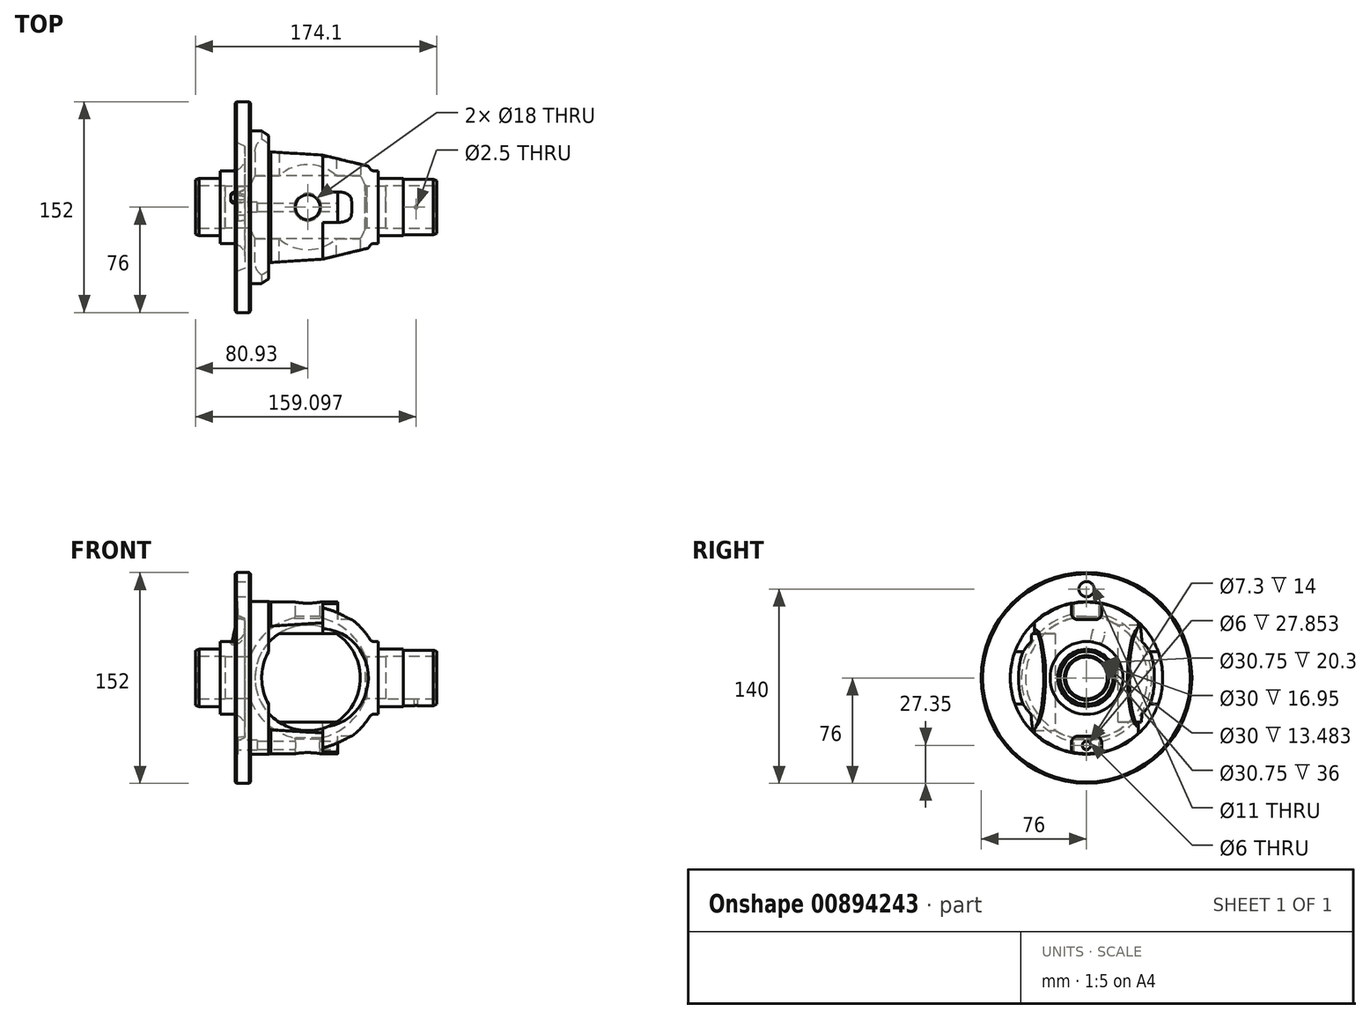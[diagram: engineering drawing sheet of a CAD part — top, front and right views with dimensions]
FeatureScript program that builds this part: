
annotation { "Feature Type Name" : "Feature", "Feature Type Description" : "" }
export const myFeature = defineFeature(function(context is Context, id is Id, definition is map)
    precondition{}
    {
        {
            var Q0;
            Q0=qCreatedBy(makeId("Front.planeOp"),FACE);
            var sketch = newSketch(context, id + "F0", { "sketchPlane" : qUnion([Q0])});
            skLineSegment(sketch, "E0", {"start": v(50.77, 21.18) * mm, "end": v(50.77, 26.25) * mm});
            skLineSegment(sketch, "E1", {"start": v(50.77, 26.25) * mm, "end": v(47.47, 26.25) * mm});
            skLineSegment(sketch, "E2", {"start": v(-78.43, 20.67) * mm, "end": v(-63.73, 20.67) * mm});
            skLineSegment(sketch, "E3", {"start": v(-63.23, 21.17) * mm, "end": v(-63.23, 26.25) * mm});
            skLineSegment(sketch, "E4", {"start": v(-63.23, 26.25) * mm, "end": v(-54.33, 26.25) * mm});
            skLineSegment(sketch, "E5", {"start": v(-41.23, 75) * mm, "end": v(-41.23, 55.5) * mm});
            skLineSegment(sketch, "E6", {"start": v(-40.73, 55) * mm, "end": v(-28.23, 55) * mm});
            skLineSegment(sketch, "E7", {"start": v(-79.93, 15.37) * mm, "end": v(-59.63, 15.37) * mm});
            skLineSegment(sketch, "E8", {"start": v(90.67, 20) * mm, "end": v(93.17, 19) * mm});
            skLineSegment(sketch, "E9", {"start": v(93.17, 16.03) * mm, "end": v(92.17, 15.38) * mm});
            skLineSegment(sketch, "E10", {"start": v(92.17, 15.38) * mm, "end": v(56.17, 15.38) * mm});
            skLineSegment(sketch, "E11", {"start": v(56.17, 15) * mm, "end": v(56.17, 15.38) * mm});
            skLineSegment(sketch, "E12", {"start": v(56.17, 15) * mm, "end": v(41.68, 15) * mm});
            skLineSegment(sketch, "E13", {"start": v(93.17, 19) * mm, "end": v(93.17, 16.03) * mm});
            skLineSegment(sketch, "E14", {"start": v(90.67, 20) * mm, "end": v(68.87, 20) * mm});
            skLineSegment(sketch, "E15", {"start": v(68.87, 20) * mm, "end": v(68.87, 20.68) * mm});
            skLineSegment(sketch, "E16", {"start": v(68.87, 20.68) * mm, "end": v(51.27, 20.68) * mm});
            skLineSegment(sketch, "E17", {"start": v(-78.43, 20.67) * mm, "end": v(-80.93, 19.67) * mm});
            skLineSegment(sketch, "E18", {"start": v(-80.93, 19.67) * mm, "end": v(-80.93, 16.02) * mm});
            skLineSegment(sketch, "E19", {"start": v(-80.93, 16.02) * mm, "end": v(-79.93, 15.37) * mm});
            skLineSegment(sketch, "E20", {"start": v(-45.33, 35.25) * mm, "end": v(-45.33, 44) * mm});
            skLineSegment(sketch, "E21", {"start": v(-52.33, 47) * mm, "end": v(-52.33, 75) * mm});
            skLineSegment(sketch, "E22", {"start": v(-59.63, 15.37) * mm, "end": v(-59.63, 15) * mm});
            skLineSegment(sketch, "E23", {"start": v(-59.63, 15) * mm, "end": v(-41.68, 15) * mm});
            skLineSegment(sketch, "E24", {"start": v(-52.33, 47) * mm, "end": v(-45.33, 44) * mm});
            skPoint(sketch, "E25.visualSharp", {"position": v(-45.33, 26.25) * mm});
            skArc(sketch, "E25.filletArc", {"start": v(-54.33, 26.25) * mm, "mid": v(-47.97, 28.89) * mm, "end": v(-45.33, 35.25) * mm});
            skLineSegment(sketch, "E26", {"start": v(-28.23, 55) * mm, "end": v(-26.73, 54.65) * mm});
            skLineSegment(sketch, "E27", {"start": v(-26.73, 54.65) * mm, "end": v(10.77, 54.65) * mm});
            skLineSegment(sketch, "E28", {"start": v(10.77, 54.65) * mm, "end": v(10.77, 52.86) * mm});
            skArc(sketch, "E29", {"start": v(44.92, 27.68) * mm, "mid": v(30.8, 42.84) * mm, "end": v(11.93, 51.4) * mm});
            skLineSegment(sketch, "E30", {"start": v(-52.33, 75) * mm, "end": v(-51.33, 76) * mm});
            skLineSegment(sketch, "E31", {"start": v(-51.33, 76) * mm, "end": v(-42.23, 76) * mm});
            skLineSegment(sketch, "E32", {"start": v(-42.23, 76) * mm, "end": v(-41.23, 75) * mm});
            skPoint(sketch, "E33.visualSharp", {"position": v(-41.23, 55) * mm});
            skArc(sketch, "E33.filletArc", {"start": v(-41.23, 55.5) * mm, "mid": v(-41.09, 55.15) * mm, "end": v(-40.73, 55) * mm});
            skPoint(sketch, "E34.visualSharp", {"position": v(-63.23, 20.67) * mm});
            skArc(sketch, "E34.filletArc", {"start": v(-63.73, 20.67) * mm, "mid": v(-63.38, 20.82) * mm, "end": v(-63.23, 21.17) * mm});
            skPoint(sketch, "E35.visualSharp", {"position": v(50.77, 20.68) * mm});
            skArc(sketch, "E35.filletArc", {"start": v(50.77, 21.18) * mm, "mid": v(50.91, 20.82) * mm, "end": v(51.27, 20.68) * mm});
            skPoint(sketch, "E36.visualSharp", {"position": v(10.77, 51.65) * mm});
            skArc(sketch, "E36.filletArc", {"start": v(10.77, 52.86) * mm, "mid": v(11.1, 51.92) * mm, "end": v(11.93, 51.4) * mm});
            skPoint(sketch, "E37.visualSharp", {"position": v(45.77, 26.25) * mm});
            skArc(sketch, "E37.filletArc", {"start": v(44.92, 27.68) * mm, "mid": v(46, 26.63) * mm, "end": v(47.47, 26.25) * mm});
            skArc(sketch, "E38", {"start": v(41.68, 15) * mm, "mid": v(0, 44.3) * mm, "end": v(-41.68, 15) * mm});
            skLineSegment(sketch, "E39", {"start": v(-80.93, 0) * mm, "end": v(93.17, 0) * mm});
            skSolve(sketch);
        }
        {
            var Q0;
            Q0=makeQuery(id+"F0.imprint","IMPRINT",FACE,{"disambiguationData":[TD([[makeQuery(id+"F0.imprint","IMPRINT",EDGE,{"derivedFrom":sQuery(id+"F0.wireOp",EDGE,"E0")}),1.0]])]});
            var Q1;
            Q1=sQuery(id+"F0.wireOp",EDGE,"E39");
            revolve(context, id + "F1", {"surfaceOperationType" : NewSurfaceOperationType.NEW, "entities" : qUnion([Q0]), "axis" : qUnion([Q1]), "revolveType" : RevolveType.FULL});
        }
        {
            var Q0;
            Q0=qCreatedBy(makeId("Front.planeOp"),FACE);
            var sketch = newSketch(context, id + "F2", { "sketchPlane" : qUnion([Q0])});
            skLineSegment(sketch, "E40", {"start": v(-20.66, -31.95) * mm, "end": v(20.66, -31.95) * mm});
            skLineSegment(sketch, "E41", {"start": v(0, 0) * mm, "end": v(0, -31.95) * mm, "construction": true});
            skArc(sketch, "E42", {"start": v(20.66, -31.95) * mm, "mid": v(0, 38.05) * mm, "end": v(-20.66, -31.95) * mm});
            skSolve(sketch);
        }
        {
            var Q0;
            Q0 = qSketchRegion(id + "F2", true);
            extrude(context, id + "F3", {"entities" : qUnion([Q0]), "operationType" : NewBodyOperationType.REMOVE, "oppositeDirection" : true, "depth" : 40 * mm, "offsetDistance" : 25 * mm});
        }
        {
            var Q0;
            Q0=qCreatedBy(makeId("Top.planeOp"),FACE);
            var sketch = newSketch(context, id + "F4", { "sketchPlane" : qUnion([Q0])});
            skLineSegment(sketch, "E43", {"start": v(-28.23, 55) * mm, "end": v(-28.23, 40.94) * mm});
            skLineSegment(sketch, "E44", {"start": v(-27.3, 39.94) * mm, "end": v(10.77, 37.5) * mm});
            skLineSegment(sketch, "E45", {"start": v(10.77, 37.5) * mm, "end": v(44.92, 29.25) * mm});
            skLineSegment(sketch, "E46", {"start": v(-28.23, 55) * mm, "end": v(44.92, 55) * mm});
            skLineSegment(sketch, "E47", {"start": v(44.92, 55) * mm, "end": v(44.92, 29.25) * mm});
            skLineSegment(sketch, "E48.MirrorCS", {"start": v(44.92, -55) * mm, "end": v(44.92, -29.25) * mm});
            skLineSegment(sketch, "E49.MirrorCS", {"start": v(-28.23, -55) * mm, "end": v(44.92, -55) * mm});
            skLineSegment(sketch, "E50.MirrorCS", {"start": v(-28.23, -55) * mm, "end": v(-28.23, -40.94) * mm});
            skLineSegment(sketch, "E51.MirrorCS", {"start": v(-27.3, -39.94) * mm, "end": v(10.77, -37.5) * mm});
            skLineSegment(sketch, "E52.MirrorCS", {"start": v(10.77, -37.5) * mm, "end": v(44.92, -29.25) * mm});
            skPoint(sketch, "E53.visualSharp", {"position": v(-28.23, 40) * mm});
            skArc(sketch, "E53.filletArc", {"start": v(-28.23, 40.94) * mm, "mid": v(-27.96, 40.25) * mm, "end": v(-27.3, 39.94) * mm});
            skPoint(sketch, "E54.visualSharp", {"position": v(-28.23, -40) * mm});
            skArc(sketch, "E54.filletArc", {"start": v(-27.3, -39.94) * mm, "mid": v(-27.96, -40.25) * mm, "end": v(-28.23, -40.94) * mm});
            skSolve(sketch);
        }
        {
            var Q0;
            Q0 = qSketchRegion(id + "F4", true);
            extrude(context, id + "F5", {"entities" : qUnion([Q0]), "operationType" : NewBodyOperationType.REMOVE, "oppositeDirection" : true, "depth" : 80 * mm, "offsetDistance" : 25 * mm, "symmetric" : true});
        }
        {
            var Q0;
            Q0=qCreatedBy(makeId("Front.planeOp"),FACE);
            var sketch = newSketch(context, id + "F6", { "sketchPlane" : qUnion([Q0])});
            skLineSegment(sketch, "E55", {"start": v(-28.23, 18.85) * mm, "end": v(-28.23, -18.85) * mm});
            skArc(sketch, "E56", {"start": v(-28.23, 18.85) * mm, "mid": v(-33.23, 0) * mm, "end": v(-28.23, -18.85) * mm});
            skSolve(sketch);
        }
        {
            var Q0;
            Q0 = qSketchRegion(id + "F6", true);
            extrude(context, id + "F7", {"entities" : qUnion([Q0]), "operationType" : NewBodyOperationType.REMOVE, "oppositeDirection" : true, "depth" : 110 * mm, "offsetDistance" : 25 * mm, "symmetric" : true});
        }
        {
            var Q0;
            Q0=qCreatedBy(makeId("Front.planeOp"),FACE);
            cPlane(context, id + "F8", {"entities" : qUnion([Q0]), "cplaneType" : CPlaneType.OFFSET, "offset" : 40 * mm, "oppositeDirection" : true, "width" : 150 * mm, "height" : 150 * mm});
        }
        {
            var Q0;
            Q0=qCreatedBy(id+"F8.planeOp",FACE);
            var sketch = newSketch(context, id + "F9", { "sketchPlane" : qUnion([Q0])});
            skArc(sketch, "E57.0", {"start": v(-27.3, 26.5) * mm, "mid": v(-38.05, 0) * mm, "end": v(-27.3, -26.5) * mm});
            skLineSegment(sketch, "E58", {"start": v(-27.3, -26.5) * mm, "end": v(-27.3, 26.5) * mm});
            skSolve(sketch);
        }
        {
            var Q0;
            Q0=makeQuery(id+"F9.imprint","IMPRINT",FACE,{"disambiguationData":[TD([[makeQuery(id+"F9.imprint","IMPRINT",EDGE,{"derivedFrom":sQuery(id+"F9.wireOp",EDGE,"E57.0")}),1.0]])]});
            var Q1;
            Q1=sQuery(id+"F9.wireOp",EDGE,"E58");
            revolve(context, id + "F10", {"operationType" : NewBodyOperationType.REMOVE, "surfaceOperationType" : NewSurfaceOperationType.NEW, "entities" : qUnion([Q0]), "axis" : qUnion([Q1]), "revolveType" : RevolveType.ONE_DIRECTION, "oppositeDirection" : true, "angle" : 90 * degree});
        }
        {
            var Q0;
            Q0=qCreatedBy(makeId("Front.planeOp"),FACE);
            var sketch = newSketch(context, id + "F11", { "sketchPlane" : qUnion([Q0])});
            skArc(sketch, "E59", {"start": v(-20.66, 31.95) * mm, "mid": v(0, -38.05) * mm, "end": v(20.66, 31.95) * mm});
            skLineSegment(sketch, "E60", {"start": v(0, 0) * mm, "end": v(0, 31.95) * mm, "construction": true});
            skLineSegment(sketch, "E61", {"start": v(20.66, 31.95) * mm, "end": v(-20.66, 31.95) * mm});
            skSolve(sketch);
        }
        {
            var Q0;
            Q0 = qSketchRegion(id + "F11", true);
            extrude(context, id + "F12", {"entities" : qUnion([Q0]), "operationType" : NewBodyOperationType.REMOVE, "depth" : 40 * mm, "offsetDistance" : 25 * mm});
        }
        {
            var Q0;
            Q0=qCreatedBy(makeId("Front.planeOp"),FACE);
            cPlane(context, id + "F13", {"entities" : qUnion([Q0]), "cplaneType" : CPlaneType.OFFSET, "offset" : 40 * mm, "width" : 150 * mm, "height" : 150 * mm});
        }
        {
            var Q0;
            Q0=qCreatedBy(id+"F13.planeOp",FACE);
            var sketch = newSketch(context, id + "F14", { "sketchPlane" : qUnion([Q0])});
            skLineSegment(sketch, "E62", {"start": v(-27.3, 26.5) * mm, "end": v(-27.3, -26.5) * mm});
            skArc(sketch, "E63", {"start": v(-27.3, 26.5) * mm, "mid": v(-38.05, 0) * mm, "end": v(-27.3, -26.5) * mm});
            skSolve(sketch);
        }
        {
            var Q0;
            Q0 = qSketchRegion(id + "F14", true);
            var Q1;
            Q1=sQuery(id+"F14.wireOp",EDGE,"E62");
            revolve(context, id + "F15", {"operationType" : NewBodyOperationType.REMOVE, "surfaceOperationType" : NewSurfaceOperationType.NEW, "entities" : qUnion([Q0]), "axis" : qUnion([Q1]), "revolveType" : RevolveType.ONE_DIRECTION, "oppositeDirection" : true, "angle" : 90 * degree});
        }
        {
            var Q0;
            Q0=makeQuery(id+"F1.opRevolve","SWEPT_FACE",FACE,{"disambiguationData":[OSD([sQuery(id+"F0.wireOp",EDGE,"E5")])]});
            var sketch = newSketch(context, id + "F16", { "sketchPlane" : qUnion([Q0])});
            skCircle(sketch, "E64", {"center": v(0, 64) * mm, "radius": 5.5 * mm});
            skSolve(sketch);
        }
        {
            var Q0;
            Q0 = qSketchRegion(id + "F16", true);
            extrude(context, id + "F17", {"entities" : qUnion([Q0]), "operationType" : NewBodyOperationType.REMOVE, "oppositeDirection" : true, "depth" : 11.1 * mm, "offsetDistance" : 25 * mm});
        }
        {
            var Q0;
            Q0=qCreatedBy(makeId("Top.planeOp"),FACE);
            var sketch = newSketch(context, id + "F18", { "sketchPlane" : qUnion([Q0])});
            skCircle(sketch, "E65", {"center": v(0, 0) * mm, "radius": 9 * mm});
            skSolve(sketch);
        }
        {
            var Q0;
            Q0 = qSketchRegion(id + "F18", true);
            extrude(context, id + "F19", {"entities" : qUnion([Q0]), "operationType" : NewBodyOperationType.REMOVE, "oppositeDirection" : true, "depth" : 110 * mm, "offsetDistance" : 25 * mm, "symmetric" : true});
        }
        {
            var Q0;
            Q0=makeQuery(id+"F5.boolean.opBoolean","SPLIT",FACE,{"disambiguationData":[OD(1.0)],"derivedFrom":makeQuery(id+"F1.opRevolve","SWEPT_FACE",FACE,{"disambiguationData":[OSD([sQuery(id+"F0.wireOp",EDGE,"E28")])]})});
            var sketch = newSketch(context, id + "F20", { "sketchPlane" : qUnion([Q0])});
            skLineSegment(sketch, "E66", {"start": v(11, 53.53) * mm, "end": v(11, 43) * mm});
            skLineSegment(sketch, "E67", {"start": v(11, 43) * mm, "end": v(-11, 43) * mm});
            skLineSegment(sketch, "E68", {"start": v(-11, 43) * mm, "end": v(-11, 53.53) * mm});
            skArc(sketch, "E69", {"start": v(11, 53.53) * mm, "mid": v(0, 54.65) * mm, "end": v(-11, 53.53) * mm});
            skPoint(sketch, "E70.visualSharp", {"position": v(-11, 43) * mm});
            skPoint(sketch, "E71.visualSharp", {"position": v(11, 43) * mm});
            skLineSegment(sketch, "E72", {"start": v(-10.57, 0) * mm, "end": v(10.57, 0) * mm, "construction": true});
            skLineSegment(sketch, "E73.MirrorCS", {"start": v(11, -43) * mm, "end": v(11, -43) * mm});
            skLineSegment(sketch, "E74.MirrorCS", {"start": v(11, -43) * mm, "end": v(-11, -43) * mm});
            skLineSegment(sketch, "E75.MirrorCS", {"start": v(-11, -43) * mm, "end": v(-11, -43) * mm});
            skLineSegment(sketch, "E76.MirrorCS", {"start": v(-11, -43) * mm, "end": v(-11, -53.53) * mm});
            skArc(sketch, "E77.MirrorCS", {"start": v(11, -53.53) * mm, "mid": v(0, -54.65) * mm, "end": v(-11, -53.53) * mm});
            skLineSegment(sketch, "E78.MirrorCS", {"start": v(11, -53.53) * mm, "end": v(11, -43) * mm});
            skSolve(sketch);
        }
        {
            var Q0;
            Q0 = qSketchRegion(id + "F20", true);
            extrude(context, id + "F21", {"entities" : qUnion([Q0]), "operationType" : NewBodyOperationType.ADD, "depth" : 11 * mm, "offsetDistance" : 25 * mm});
        }
        {
            var Q0;
            Q0=makeQuery(id+"F21.opExtrude","CAP_FACE",FACE,{"disambiguationData":[OSD([sQuery(id+"F20.wireOp",EDGE,"E66"),sQuery(id+"F20.wireOp",EDGE,"E67"),sQuery(id+"F20.wireOp",EDGE,"E68"),sQuery(id+"F20.wireOp",EDGE,"E69")])],"isStart":false});
            var sketch = newSketch(context, id + "F22", { "sketchPlane" : qUnion([Q0])});
            skLineSegment(sketch, "E79", {"start": v(6.22, 42) * mm, "end": v(-6.21, 42) * mm});
            skLineSegment(sketch, "E80", {"start": v(11, 46.79) * mm, "end": v(11, 46.79) * mm});
            skLineSegment(sketch, "E81", {"start": v(-11, 46.78) * mm, "end": v(-11, 46.79) * mm});
            skArc(sketch, "E82.filletArc", {"start": v(-11, 46.78) * mm, "mid": v(-9.6, 43.4) * mm, "end": v(-6.21, 42) * mm});
            skArc(sketch, "E83.filletArc", {"start": v(6.22, 42) * mm, "mid": v(9.6, 43.4) * mm, "end": v(11, 46.79) * mm});
            skArc(sketch, "E84.0", {"start": v(11, 46.79) * mm, "mid": v(0, 48.06) * mm, "end": v(-11, 46.79) * mm});
            skArc(sketch, "E85.MirrorCS", {"start": v(11, -46.79) * mm, "mid": v(0, -48.06) * mm, "end": v(-11, -46.79) * mm});
            skLineSegment(sketch, "E86", {"start": v(-6.21, -42) * mm, "end": v(6.21, -42) * mm});
            skLineSegment(sketch, "E87", {"start": v(11, -46.79) * mm, "end": v(11, -46.79) * mm});
            skLineSegment(sketch, "E88", {"start": v(-11, -46.79) * mm, "end": v(-11, -46.79) * mm});
            skPoint(sketch, "E89.visualSharp", {"position": v(-11, -42) * mm});
            skArc(sketch, "E89.filletArc", {"start": v(-6.21, -42) * mm, "mid": v(-9.6, -43.4) * mm, "end": v(-11, -46.79) * mm});
            skPoint(sketch, "E90.visualSharp", {"position": v(11, -42) * mm});
            skArc(sketch, "E90.filletArc", {"start": v(11, -46.79) * mm, "mid": v(9.6, -43.4) * mm, "end": v(6.21, -42) * mm});
            skSolve(sketch);
        }
        {
            var Q0;
            Q0 = qSketchRegion(id + "F22", true);
            extrude(context, id + "F23", {"entities" : qUnion([Q0]), "operationType" : NewBodyOperationType.REMOVE, "depth" : 12 * mm, "offsetDistance" : 25 * mm});
        }
        {
            var Q0;
            Q0=makeQuery(id+"F23.boolean.opBoolean","MERGE",FACE,{"derivedFrom":[makeQuery(id+"F21.opExtrude","CAP_FACE",FACE,{"disambiguationData":[OSD([sQuery(id+"F20.wireOp",EDGE,"E74.MirrorCS"),sQuery(id+"F20.wireOp",EDGE,"E76.MirrorCS"),sQuery(id+"F20.wireOp",EDGE,"E77.MirrorCS"),sQuery(id+"F20.wireOp",EDGE,"E78.MirrorCS")])],"isStart":false})],"fromTools":[makeQuery(id+"F23.opExtrude","CAP_FACE",FACE,{"disambiguationData":[OSD([sQuery(id+"F22.wireOp",EDGE,"E85.MirrorCS"),sQuery(id+"F22.wireOp",EDGE,"E86"),sQuery(id+"F22.wireOp",EDGE,"E87"),sQuery(id+"F22.wireOp",EDGE,"E88"),sQuery(id+"F22.wireOp",EDGE,"E89.filletArc"),sQuery(id+"F22.wireOp",EDGE,"E90.filletArc")])],"isStart":true})]});
            var sketch = newSketch(context, id + "F24", { "sketchPlane" : qUnion([Q0])});
            skCircle(sketch, "E91", {"center": v(0, -48.65) * mm, "radius": 3 * mm});
            skSolve(sketch);
        }
        {
            var Q0;
            Q0 = qSketchRegion(id + "F24", true);
            extrude(context, id + "F25", {"entities" : qUnion([Q0]), "operationType" : NewBodyOperationType.REMOVE, "endBound" : BoundingType.THROUGH_ALL, "oppositeDirection" : true, "depth" : 25 * mm, "offsetDistance" : 25 * mm});
        }
        {
            var Q0;
            Q0=makeQuery(id+"F1.opRevolve","SWEPT_FACE",FACE,{"disambiguationData":[OSD([sQuery(id+"F0.wireOp",EDGE,"E21")])]});
            var sketch = newSketch(context, id + "F26", { "sketchPlane" : qUnion([Q0])});
            skCircle(sketch, "E92", {"center": v(0, -48.65) * mm, "radius": 3.65 * mm});
            skSolve(sketch);
        }
        {
            var Q0;
            Q0 = qSketchRegion(id + "F26", true);
            extrude(context, id + "F27", {"entities" : qUnion([Q0]), "operationType" : NewBodyOperationType.REMOVE, "oppositeDirection" : true, "depth" : 16 * mm, "offsetDistance" : 25 * mm});
        }
        {
            var Q0;
            Q0=qCreatedBy(makeId("Top.planeOp"),FACE);
            var sketch = newSketch(context, id + "F28", { "sketchPlane" : qUnion([Q0])});
            skCircle(sketch, "E93", {"center": v(78.17, 0) * mm, "radius": 1.25 * mm});
            skSolve(sketch);
        }
        {
            var Q0;
            Q0 = qSketchRegion(id + "F28", true);
            extrude(context, id + "F29", {"entities" : qUnion([Q0]), "operationType" : NewBodyOperationType.REMOVE, "endBound" : BoundingType.THROUGH_ALL, "oppositeDirection" : true, "depth" : 25 * mm, "offsetDistance" : 25 * mm});
        }
        {
            var Q0;
            Q0=makeQuery(id+"F1.opRevolve","SWEPT_FACE",FACE,{"disambiguationData":[OSD([sQuery(id+"F0.wireOp",EDGE,"E21")])]});
            var sketch = newSketch(context, id + "F30", { "sketchPlane" : qUnion([Q0])});
            skLineSegment(sketch, "E94.0", {"start": v(-6.22, 42) * mm, "end": v(6.21, 42) * mm});
            skArc(sketch, "E95.0", {"start": v(6.21, 42) * mm, "mid": v(9.6, 43.4) * mm, "end": v(11, 46.78) * mm});
            skArc(sketch, "E96.0", {"start": v(-11, 46.79) * mm, "mid": v(-9.6, 43.4) * mm, "end": v(-6.22, 42) * mm});
            skLineSegment(sketch, "E97.0", {"start": v(-11, 53.53) * mm, "end": v(-11, 46.79) * mm});
            skLineSegment(sketch, "E98.0", {"start": v(11, 46.79) * mm, "end": v(11, 53.53) * mm});
            skLineSegment(sketch, "E99.0", {"start": v(6.21, -42) * mm, "end": v(-6.21, -42) * mm});
            skArc(sketch, "E100.0", {"start": v(-6.21, -42) * mm, "mid": v(-9.6, -43.4) * mm, "end": v(-11, -46.79) * mm});
            skArc(sketch, "E101.0", {"start": v(11, -46.78) * mm, "mid": v(9.6, -43.4) * mm, "end": v(6.21, -42) * mm});
            skLineSegment(sketch, "E102.0", {"start": v(11, -46.79) * mm, "end": v(11, -53.53) * mm});
            skLineSegment(sketch, "E103.0", {"start": v(-11, -53.53) * mm, "end": v(-11, -46.79) * mm});
            skLineSegment(sketch, "E104", {"start": v(-11, 53.53) * mm, "end": v(11, 53.53) * mm});
            skLineSegment(sketch, "E105", {"start": v(-11, -53.53) * mm, "end": v(11, -53.53) * mm});
            skArc(sketch, "E106.0", {"start": v(-3.2, -46.9) * mm, "mid": v(0, -52.3) * mm, "end": v(3.2, -46.9) * mm});
            skArc(sketch, "E107.0", {"start": v(3.2, -46.9) * mm, "mid": v(0, -45) * mm, "end": v(-3.2, -46.9) * mm});
            skSolve(sketch);
        }
        {
            var Q0;
            {var subQ0=sQuery(id+"F30.wireOp",EDGE,"E94.0");Q0=makeQuery(id+"F30.imprint","IMPRINT",FACE,{"disambiguationData":[TD([[makeQuery(id+"F30.imprint","IMPRINT",EDGE,{"derivedFrom":subQ0}),1.0]])]});}
            var Q1;
            {var subQ2=sQuery(id+"F30.wireOp",EDGE,"E99.0");Q1=makeQuery(id+"F30.imprint","IMPRINT",FACE,{"disambiguationData":[TD([[makeQuery(id+"F30.imprint","IMPRINT",EDGE,{"derivedFrom":subQ2}),1.0]])]});}
            var Q2;
            Q2=makeQuery(id+"F1.opRevolve","SWEPT_FACE",FACE,{"disambiguationData":[OSD([sQuery(id+"F0.wireOp",EDGE,"E20")])]});
            extrude(context, id + "F31", {"entities" : qUnion([Q0, Q1]), "operationType" : NewBodyOperationType.ADD, "endBound" : BoundingType.UP_TO_SURFACE, "oppositeDirection" : true, "depth" : 25 * mm, "endBoundEntityFace" : qUnion([Q2]), "offsetDistance" : 25 * mm});
        }
        {
            var Q0;
            Q0=makeQuery(id+"F31.opExtrude","CAP_EDGE",EDGE,{"disambiguationData":[OSD([sQuery(id+"F30.wireOp",EDGE,"E99.0")])],"isStart":true});
            var Q1;
            Q1=makeQuery(id+"F31.opExtrude","CAP_EDGE",EDGE,{"disambiguationData":[OSD([sQuery(id+"F30.wireOp",EDGE,"E94.0")])],"isStart":true});
            chamfer(context, id + "F32", {"entities" : qUnion([Q0, Q1]), "chamferType" : ChamferType.TWO_OFFSETS, "width1" : 1 * mm, "oppositeDirection" : false, "width2" : 7 * mm, "tangentPropagation" : true});
        }
        {
            var Q0;
            {var subQ0=sQuery(id+"F0.wireOp",EDGE,"E24");var subQ1=sQuery(id+"F0.wireOp",EDGE,"E21");Q0=makeQuery(id+"F31.boolean.opBoolean","MERGE",FACE,{"derivedFrom":[makeQuery(id+"F1.opRevolve","SWEPT_FACE",FACE,{"disambiguationData":[OSD([subQ1])]}),makeQuery(id+"F31.opExtrude","CAP_FACE",FACE,{"disambiguationData":[OSD([subQ1,subQ0,sQuery(id+"F30.wireOp",EDGE,"E94.0"),sQuery(id+"F30.wireOp",EDGE,"E95.0"),sQuery(id+"F30.wireOp",EDGE,"E96.0")])],"isStart":true}),makeQuery(id+"F31.opExtrude","CAP_FACE",FACE,{"disambiguationData":[OSD([subQ1,subQ0,sQuery(id+"F30.wireOp",EDGE,"E99.0"),sQuery(id+"F30.wireOp",EDGE,"E100.0"),sQuery(id+"F30.wireOp",EDGE,"E101.0"),sQuery(id+"F30.wireOp",EDGE,"E107.0")])],"isStart":true})]});}
            var sketch = newSketch(context, id + "F33", { "sketchPlane" : qUnion([Q0])});
            skLineSegment(sketch, "E108", {"start": v(4.9, -55) * mm, "end": v(-4.9, -55) * mm});
            skLineSegment(sketch, "E109", {"start": v(9.9, -50) * mm, "end": v(9.9, -42) * mm});
            skLineSegment(sketch, "E110", {"start": v(-9.9, -50) * mm, "end": v(-9.9, -42) * mm});
            skLineSegment(sketch, "E111", {"start": v(-10.43, 0) * mm, "end": v(10.43, 0) * mm});
            skPoint(sketch, "E112.visualSharp", {"position": v(-9.9, -55) * mm});
            skArc(sketch, "E112.filletArc", {"start": v(-9.9, -50) * mm, "mid": v(-8.44, -53.54) * mm, "end": v(-4.9, -55) * mm});
            skPoint(sketch, "E113.visualSharp", {"position": v(9.9, -55) * mm});
            skArc(sketch, "E113.filletArc", {"start": v(4.9, -55) * mm, "mid": v(8.44, -53.54) * mm, "end": v(9.9, -50) * mm});
            skArc(sketch, "E114.MirrorCS", {"start": v(4.9, 55) * mm, "mid": v(8.44, 53.54) * mm, "end": v(9.9, 50) * mm});
            skLineSegment(sketch, "E115.MirrorCS", {"start": v(4.9, 55) * mm, "end": v(-4.9, 55) * mm});
            skArc(sketch, "E116.MirrorCS", {"start": v(-9.9, 50) * mm, "mid": v(-8.44, 53.54) * mm, "end": v(-4.9, 55) * mm});
            skLineSegment(sketch, "E117", {"start": v(9.9, -42) * mm, "end": v(-9.9, -42) * mm});
            skLineSegment(sketch, "E118.MirrorCS", {"start": v(9.9, 50) * mm, "end": v(9.9, 42) * mm});
            skLineSegment(sketch, "E119.MirrorCS", {"start": v(9.9, 42) * mm, "end": v(-9.9, 42) * mm});
            skLineSegment(sketch, "E120.MirrorCS", {"start": v(-9.9, 50) * mm, "end": v(-9.9, 42) * mm});
            skSolve(sketch);
        }
        {
            var Q0;
            Q0 = qSketchRegion(id + "F33", true);
            extrude(context, id + "F34", {"entities" : qUnion([Q0]), "operationType" : NewBodyOperationType.REMOVE, "oppositeDirection" : true, "depth" : 2 * mm, "offsetDistance" : 25 * mm});
        }
        {
            var Q0;
            Q0=qCreatedBy(makeId("Front.planeOp"),FACE);
            var sketch = newSketch(context, id + "F35", { "sketchPlane" : qUnion([Q0])});
            skLineSegment(sketch, "E121", {"start": v(0, 0) * mm, "end": v(-24.58, 0) * mm, "construction": true});
            skSolve(sketch);
        }
        {
            var Q0;
            Q0=sQuery(id+"F35.wireOp",EDGE,"E121");
            var Q1;
            Q1=qCreatedBy(id+"F13.planeOp",FACE);
            cPlane(context, id + "F36", {"entities" : qUnion([Q0, Q1]), "cplaneType" : CPlaneType.LINE_ANGLE, "offset" : 25 * mm, "angle" : 15 * degree, "width" : 150 * mm, "height" : 150 * mm});
        }
        {
            var Q0;
            Q0=qCreatedBy(id+"F36.planeOp",FACE);
            var sketch = newSketch(context, id + "F37", { "sketchPlane" : qUnion([Q0])});
            skLineSegment(sketch, "E122", {"start": v(54.73, 26.25) * mm, "end": v(50.33, 47) * mm});
            skSolve(sketch);
        }
        {
            var Q0;
            Q0=sQuery(id+"F35.wireOp",EDGE,"E121");
            var Q1;
            Q1=qCreatedBy(id+"F36.planeOp",FACE);
            cPlane(context, id + "F38", {"entities" : qUnion([Q0, Q1]), "cplaneType" : CPlaneType.LINE_ANGLE, "offset" : 25 * mm, "angle" : 90 * degree, "width" : 150 * mm, "height" : 150 * mm});
        }
        {
            var Q0;
            Q0=qCreatedBy(id+"F38.planeOp",FACE);
            cPlane(context, id + "F39", {"entities" : qUnion([Q0]), "cplaneType" : CPlaneType.OFFSET, "offset" : 26 * mm, "width" : 150 * mm, "height" : 150 * mm});
        }
        {
            var Q0;
            Q0=qCreatedBy(id+"F39.planeOp",FACE);
            var sketch = newSketch(context, id + "F40", { "sketchPlane" : qUnion([Q0])});
            skLineSegment(sketch, "E123", {"start": v(-54.73, -2.1) * mm, "end": v(-54.73, 2.1) * mm});
            skLineSegment(sketch, "E124", {"start": v(-53.84, 3.1) * mm, "end": v(-45.33, 4) * mm});
            skLineSegment(sketch, "E125", {"start": v(-53.84, -3.1) * mm, "end": v(-45.33, -4) * mm});
            skLineSegment(sketch, "E126", {"start": v(-45.33, -4) * mm, "end": v(-45.33, 4) * mm});
            skPoint(sketch, "E127.visualSharp", {"position": v(-54.73, 3) * mm});
            skArc(sketch, "E127.filletArc", {"start": v(-53.84, 3.1) * mm, "mid": v(-54.48, 2.77) * mm, "end": v(-54.73, 2.1) * mm});
            skPoint(sketch, "E128.visualSharp", {"position": v(-54.73, -3) * mm});
            skArc(sketch, "E128.filletArc", {"start": v(-54.73, -2.1) * mm, "mid": v(-54.48, -2.77) * mm, "end": v(-53.84, -3.1) * mm});
            skSolve(sketch);
        }
        {
            var Q0;
            Q0 = qSketchRegion(id + "F40", true);
            var Q1;
            Q1=sQuery(id+"F37.wireOp",EDGE,"E122");
            sweep(context, id + "F41", {"operationType" : NewBodyOperationType.ADD, "profiles" : qUnion([Q0]), "path" : qUnion([Q1])});
        }
        {
            var Q0;
            Q0=makeQuery(id+"F41.boolean.opBoolean","INTERSECT",EDGE,{"derivedFrom":[makeQuery(id+"F1.opRevolve","SWEPT_FACE",FACE,{"disambiguationData":[OSD([sQuery(id+"F0.wireOp",EDGE,"E20")])]}),makeQuery(id+"F41.opSweep","SWEPT_FACE",FACE,{"disambiguationData":[OSD([sQuery(id+"F37.wireOp",EDGE,"E122"),sQuery(id+"F40.wireOp",EDGE,"E125")])]})]});
            var Q1;
            Q1=makeQuery(id+"F41.boolean.opBoolean","INTERSECT",EDGE,{"derivedFrom":[makeQuery(id+"F1.opRevolve","SWEPT_FACE",FACE,{"disambiguationData":[OSD([sQuery(id+"F0.wireOp",EDGE,"E25.filletArc")])]}),makeQuery(id+"F41.opSweep","SWEPT_FACE",FACE,{"disambiguationData":[OSD([sQuery(id+"F37.wireOp",EDGE,"E122"),sQuery(id+"F40.wireOp",EDGE,"E124")])]})]});
            var Q2;
            Q2=makeQuery(id+"F41.boolean.opBoolean","INTERSECT",EDGE,{"derivedFrom":[makeQuery(id+"F1.opRevolve","SWEPT_FACE",FACE,{"disambiguationData":[OSD([sQuery(id+"F0.wireOp",EDGE,"E4")])]}),makeQuery(id+"F41.opSweep","SWEPT_FACE",FACE,{"disambiguationData":[OSD([sQuery(id+"F37.wireOp",EDGE,"E122"),sQuery(id+"F40.wireOp",EDGE,"E123")])]})]});
            fillet(context, id + "F42", {"entities" : qUnion([Q0, Q1, Q2]), "radius" : 1 * mm, "tangentPropagation" : true, "allowEdgeOverflow" : false});
        }
        {
            var Q0;
            Q0=makeQuery(id+"F1.opRevolve","SWEPT_EDGE",EDGE,{"disambiguationData":[OSD([sQuery(id+"F0.wireOp",EDGE,"E23"),sQuery(id+"F0.wireOp",EDGE,"E38")])]});
            var Q1;
            Q1=makeQuery(id+"F1.opRevolve","SWEPT_EDGE",EDGE,{"disambiguationData":[OSD([sQuery(id+"F0.wireOp",EDGE,"E12"),sQuery(id+"F0.wireOp",EDGE,"E38")])]});
            var Q2;
            Q2=makeQuery(id+"F19.boolean.opBoolean","INTERSECT",EDGE,{"disambiguationData":[OD(0.0)],"derivedFrom":[makeQuery(id+"F3.boolean.opBoolean","SPLIT",FACE,{"disambiguationData":[TD([makeQuery(id+"F1.opRevolve","SWEPT_FACE",FACE,{"disambiguationData":[OSD([sQuery(id+"F0.wireOp",EDGE,"E12")])]})])],"derivedFrom":makeQuery(id+"F1.opRevolve","SWEPT_FACE",FACE,{"disambiguationData":[OSD([sQuery(id+"F0.wireOp",EDGE,"E38")])]})}),makeQuery(id+"F19.opExtrude","SWEPT_FACE",FACE,{"disambiguationData":[OSD([sQuery(id+"F18.wireOp",EDGE,"E65")])]})]});
            var Q3;
            Q3=makeQuery(id+"F19.boolean.opBoolean","INTERSECT",EDGE,{"disambiguationData":[OD(1.0)],"derivedFrom":[makeQuery(id+"F3.boolean.opBoolean","SPLIT",FACE,{"disambiguationData":[TD([makeQuery(id+"F1.opRevolve","SWEPT_FACE",FACE,{"disambiguationData":[OSD([sQuery(id+"F0.wireOp",EDGE,"E12")])]})])],"derivedFrom":makeQuery(id+"F1.opRevolve","SWEPT_FACE",FACE,{"disambiguationData":[OSD([sQuery(id+"F0.wireOp",EDGE,"E38")])]})}),makeQuery(id+"F19.opExtrude","SWEPT_FACE",FACE,{"disambiguationData":[OSD([sQuery(id+"F18.wireOp",EDGE,"E65")])]})]});
            chamfer(context, id + "F43", {"entities" : qUnion([Q0, Q1, Q2, Q3]), "width" : 1 * mm, "tangentPropagation" : true});
        }
    });
